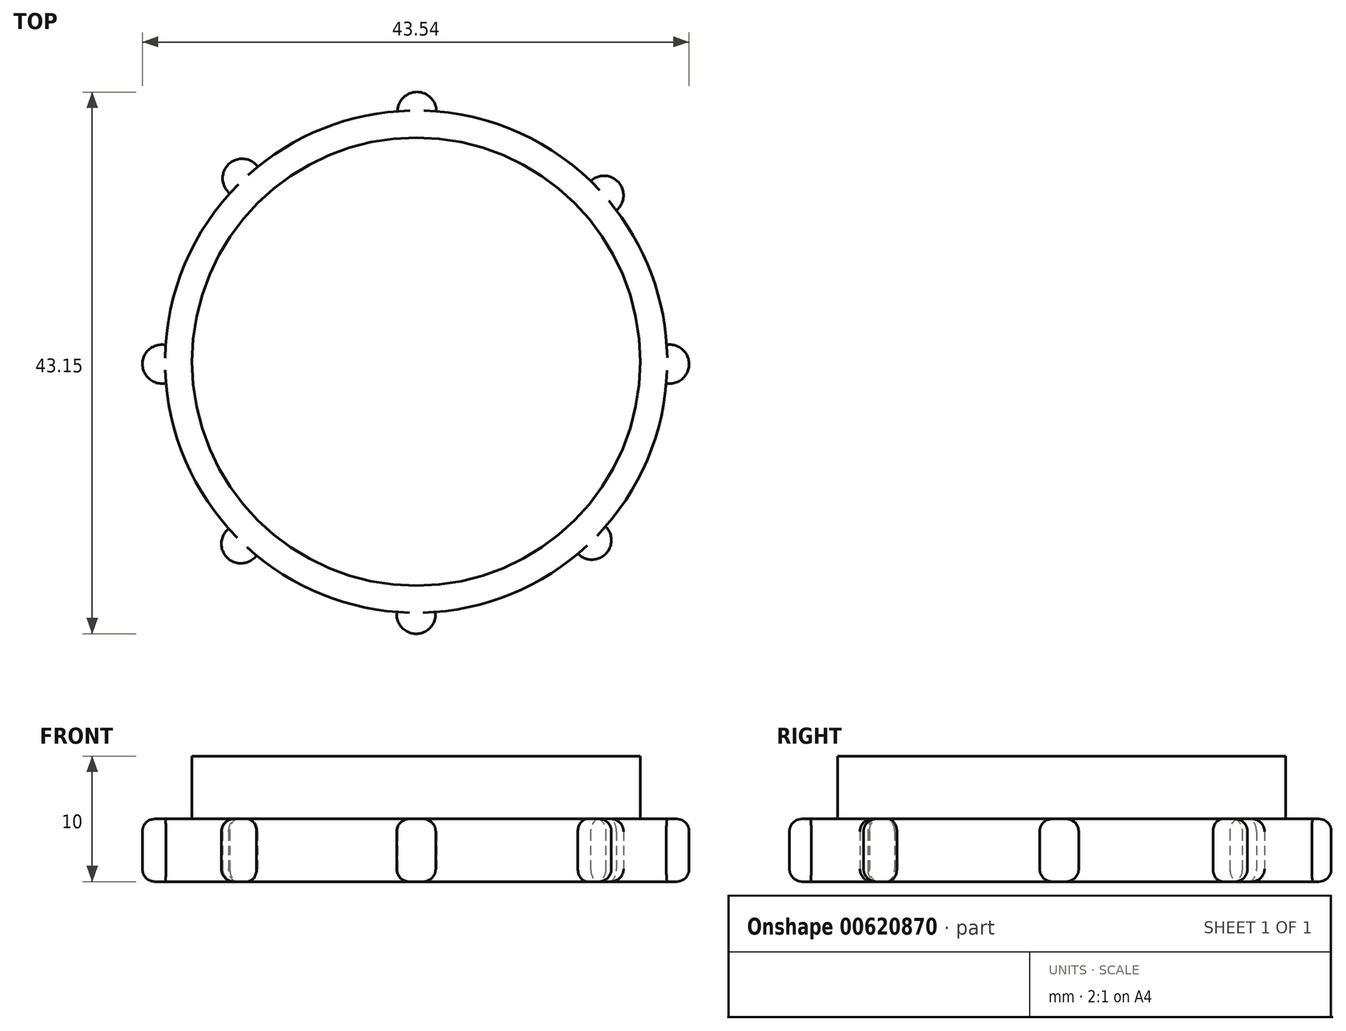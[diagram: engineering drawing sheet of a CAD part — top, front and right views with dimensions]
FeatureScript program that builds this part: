
annotation { "Feature Type Name" : "Feature", "Feature Type Description" : "" }
export const myFeature = defineFeature(function(context is Context, id is Id, definition is map)
    precondition{}
    {
        {
            var Q0;
            Q0=qCreatedBy(makeId("Top.planeOp"),FACE);
            var sketch = newSketch(context, id + "F0", { "sketchPlane" : qUnion([Q0])});
            skCircle(sketch, "E0", {"center": v(0, 0) * mm, "radius": 20 * mm});
            skSolve(sketch);
        }
        {
            var Q0;
            Q0 = qSketchRegion(id + "F0", true);
            extrude(context, id + "F1", {"entities" : qUnion([Q0]), "depth" : 5 * mm, "offsetDistance" : 25 * mm});
        }
        {
            var Q0;
            Q0=makeQuery(id+"F1.opExtrude","CAP_FACE",FACE,{"disambiguationData":[OSD([sQuery(id+"F0.wireOp",EDGE,"E0")])],"isStart":false});
            var sketch = newSketch(context, id + "F2", { "sketchPlane" : qUnion([Q0])});
            skCircle(sketch, "E1", {"center": v(0, 0) * mm, "radius": 17.85 * mm});
            skSolve(sketch);
        }
        {
            var Q0;
            Q0 = qSketchRegion(id + "F2", true);
            extrude(context, id + "F3", {"entities" : qUnion([Q0]), "operationType" : NewBodyOperationType.ADD, "depth" : 5 * mm, "offsetDistance" : 25 * mm});
        }
        {
            var Q0;
            Q0=makeQuery(id+"F0.imprint","IMPRINT",FACE,{"disambiguationData":[TD([[makeQuery(id+"F0.imprint","IMPRINT",EDGE,{"derivedFrom":sQuery(id+"F0.wireOp",EDGE,"E0")}),1.0]])]});
            var sketch = newSketch(context, id + "F4", { "sketchPlane" : qUnion([Q0])});
            skCircle(sketch, "E2", {"center": v(0, -20.12) * mm, "radius": 1.55 * mm});
            skCircle(sketch, "E3", {"center": v(14, -14.22) * mm, "radius": 1.55 * mm});
            skCircle(sketch, "E4", {"center": v(20.19, -0.2) * mm, "radius": 1.55 * mm});
            skCircle(sketch, "E5", {"center": v(14.96, 13.25) * mm, "radius": 1.55 * mm});
            skCircle(sketch, "E6", {"center": v(0.07, 19.93) * mm, "radius": 1.55 * mm});
            skCircle(sketch, "E7", {"center": v(-13.87, 14.6) * mm, "radius": 1.55 * mm});
            skCircle(sketch, "E8", {"center": v(-20.25, -0.2) * mm, "radius": 1.55 * mm});
            skCircle(sketch, "E9", {"center": v(-13.96, -14.51) * mm, "radius": 1.55 * mm});
            skSolve(sketch);
        }
        {
            var Q0;
            Q0 = qSketchRegion(id + "F4", true);
            var Q1;
            Q1 = qSketchRegion(id + "F2", true);
            extrude(context, id + "F5", {"entities" : qUnion([Q0, Q1]), "operationType" : NewBodyOperationType.ADD, "depth" : 5 * mm, "offsetDistance" : 25 * mm});
        }
        {
            var Q0;
            Q0=makeQuery(id+"F5.opExtrude","CAP_EDGE",EDGE,{"disambiguationData":[OSD([sQuery(id+"F4.wireOp",EDGE,"E9")])],"isStart":true});
            var Q1;
            Q1=makeQuery(id+"F5.opExtrude","CAP_EDGE",EDGE,{"disambiguationData":[OSD([sQuery(id+"F4.wireOp",EDGE,"E2")])],"isStart":true});
            var Q2;
            Q2=makeQuery(id+"F5.opExtrude","CAP_EDGE",EDGE,{"disambiguationData":[OSD([sQuery(id+"F4.wireOp",EDGE,"E3")])],"isStart":true});
            var Q3;
            Q3=makeQuery(id+"F5.opExtrude","CAP_EDGE",EDGE,{"disambiguationData":[OSD([sQuery(id+"F4.wireOp",EDGE,"E4")])],"isStart":true});
            var Q4;
            Q4=makeQuery(id+"F5.opExtrude","CAP_EDGE",EDGE,{"disambiguationData":[OSD([sQuery(id+"F4.wireOp",EDGE,"E5")])],"isStart":true});
            var Q5;
            Q5=makeQuery(id+"F5.opExtrude","CAP_EDGE",EDGE,{"disambiguationData":[OSD([sQuery(id+"F4.wireOp",EDGE,"E6")])],"isStart":true});
            var Q6;
            Q6=makeQuery(id+"F5.opExtrude","CAP_EDGE",EDGE,{"disambiguationData":[OSD([sQuery(id+"F4.wireOp",EDGE,"E7")])],"isStart":true});
            var Q7;
            Q7=makeQuery(id+"F5.opExtrude","CAP_EDGE",EDGE,{"disambiguationData":[OSD([sQuery(id+"F4.wireOp",EDGE,"E8")])],"isStart":true});
            var Q8;
            Q8=makeQuery(id+"F5.opExtrude","CAP_EDGE",EDGE,{"disambiguationData":[OSD([sQuery(id+"F4.wireOp",EDGE,"E8")])],"isStart":false});
            var Q9;
            Q9=makeQuery(id+"F5.opExtrude","CAP_EDGE",EDGE,{"disambiguationData":[OSD([sQuery(id+"F4.wireOp",EDGE,"E9")])],"isStart":false});
            var Q10;
            Q10=makeQuery(id+"F5.opExtrude","CAP_EDGE",EDGE,{"disambiguationData":[OSD([sQuery(id+"F4.wireOp",EDGE,"E2")])],"isStart":false});
            var Q11;
            Q11=makeQuery(id+"F5.opExtrude","CAP_EDGE",EDGE,{"disambiguationData":[OSD([sQuery(id+"F4.wireOp",EDGE,"E3")])],"isStart":false});
            var Q12;
            Q12=makeQuery(id+"F5.opExtrude","CAP_EDGE",EDGE,{"disambiguationData":[OSD([sQuery(id+"F4.wireOp",EDGE,"E4")])],"isStart":false});
            var Q13;
            Q13=makeQuery(id+"F5.opExtrude","CAP_EDGE",EDGE,{"disambiguationData":[OSD([sQuery(id+"F4.wireOp",EDGE,"E5")])],"isStart":false});
            var Q14;
            Q14=makeQuery(id+"F5.opExtrude","CAP_EDGE",EDGE,{"disambiguationData":[OSD([sQuery(id+"F4.wireOp",EDGE,"E6")])],"isStart":false});
            var Q15;
            Q15=makeQuery(id+"F5.opExtrude","CAP_EDGE",EDGE,{"disambiguationData":[OSD([sQuery(id+"F4.wireOp",EDGE,"E7")])],"isStart":false});
            fillet(context, id + "F6", {"entities" : qUnion([Q0, Q1, Q2, Q3, Q4, Q5, Q6, Q7, Q8, Q9, Q10, Q11, Q12, Q13, Q14, Q15]), "radius" : 1 * mm, "tangentPropagation" : true, "allowEdgeOverflow" : false});
        }
    });
